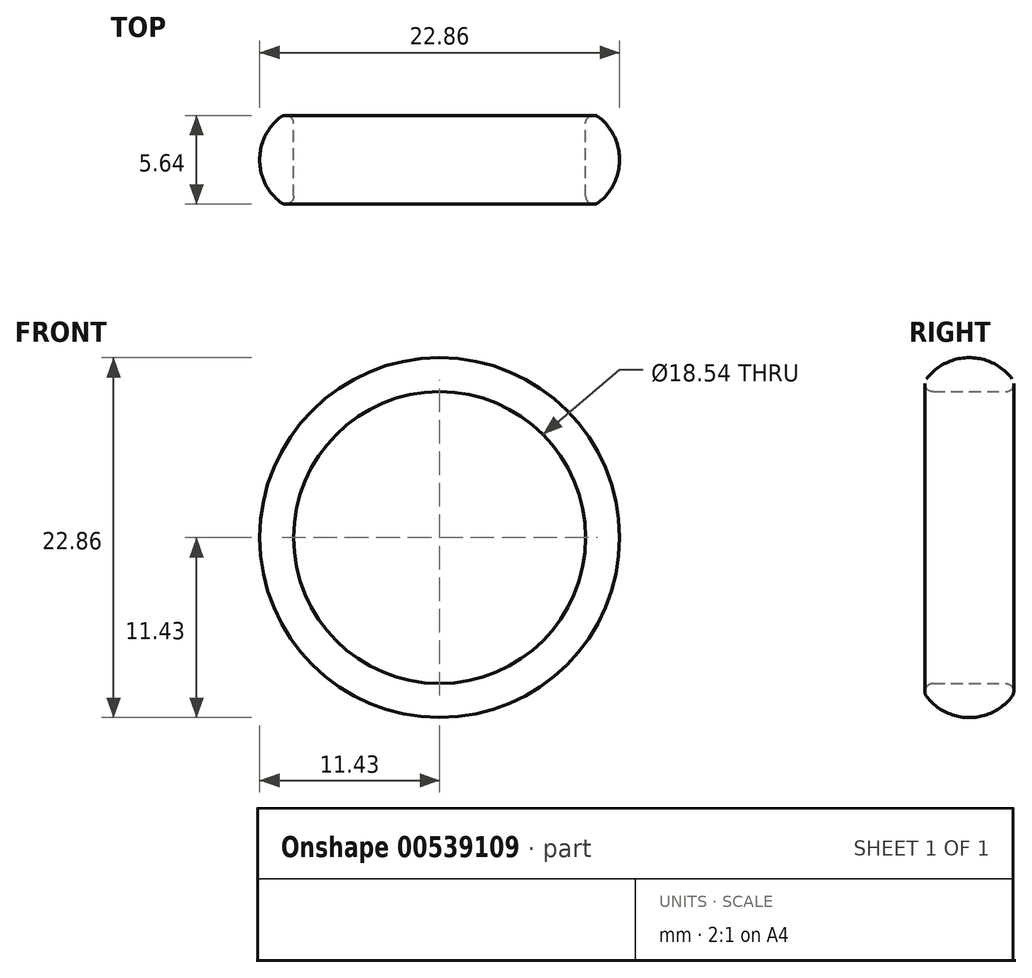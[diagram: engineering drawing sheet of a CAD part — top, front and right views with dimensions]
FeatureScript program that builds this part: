
annotation { "Feature Type Name" : "Feature", "Feature Type Description" : "" }
export const myFeature = defineFeature(function(context is Context, id is Id, definition is map)
    precondition{}
    {
        {
            var Q0;
            Q0=qCreatedBy(makeId("Front.planeOp"),FACE);
            var sketch = newSketch(context, id + "F0", { "sketchPlane" : qUnion([Q0])});
            skCircle(sketch, "E0", {"center": v(0, 0) * mm, "radius": 9.27 * mm});
            skCircle(sketch, "E1", {"center": v(0, 0) * mm, "radius": 11.43 * mm});
            skSolve(sketch);
        }
        {
            var Q0;
            Q0=makeQuery(id+"F0.imprint","IMPRINT",FACE,{"disambiguationData":[TD([[makeQuery(id+"F0.imprint","IMPRINT",EDGE,{"derivedFrom":sQuery(id+"F0.wireOp",EDGE,"E0")}),-1.0]])]});
            extrude(context, id + "F1", {"entities" : qUnion([Q0]), "depth" : 3.17 * mm, "offsetDistance" : 25.4 * mm});
        }
        {
            var Q0;
            Q0=makeQuery(id+"F1.opExtrude","CAP_EDGE",EDGE,{"disambiguationData":[OSD([sQuery(id+"F0.wireOp",EDGE,"E1")])],"isStart":false});
            fillet(context, id + "F2", {"entities" : qUnion([Q0]), "radius" : 3.4 * mm, "tangentPropagation" : true, "allowEdgeOverflow" : false});
        }
        {
            var Q0;
            Q0=makeQuery(id+"F2.opFillet","BLEND_EDGE",EDGE,{"blendedFrom":[makeQuery(id+"F1.opExtrude","CAP_EDGE",EDGE,{"disambiguationData":[OSD([sQuery(id+"F0.wireOp",EDGE,"E1")])],"isStart":false}),makeQuery(id+"F1.opExtrude","SWEPT_FACE",FACE,{"disambiguationData":[OSD([sQuery(id+"F0.wireOp",EDGE,"E0")])]})],"blendedInto":[makeQuery(id+"F1.opExtrude","SWEPT_FACE",FACE,{"disambiguationData":[OSD([sQuery(id+"F0.wireOp",EDGE,"E0")])]})]});
            fillet(context, id + "F3", {"entities" : qUnion([Q0]), "radius" : 0.5 * mm, "tangentPropagation" : true, "allowEdgeOverflow" : false});
        }
        {
            var Q0;
            Q0=makeQuery(id+"F1.opExtrude","SWEPT_BODY",BODY,{"disambiguationData":[OSD([sQuery(id+"F0.wireOp",EDGE,"E0"),sQuery(id+"F0.wireOp",EDGE,"E1")])]});
            var Q1;
            Q1=qCreatedBy(makeId("Front.planeOp"),FACE);
            mirror(context, id + "F4", {"operationType" : NewBodyOperationType.ADD, "entities" : qUnion([Q0]), "mirrorPlane" : qUnion([Q1])});
        }
    });
